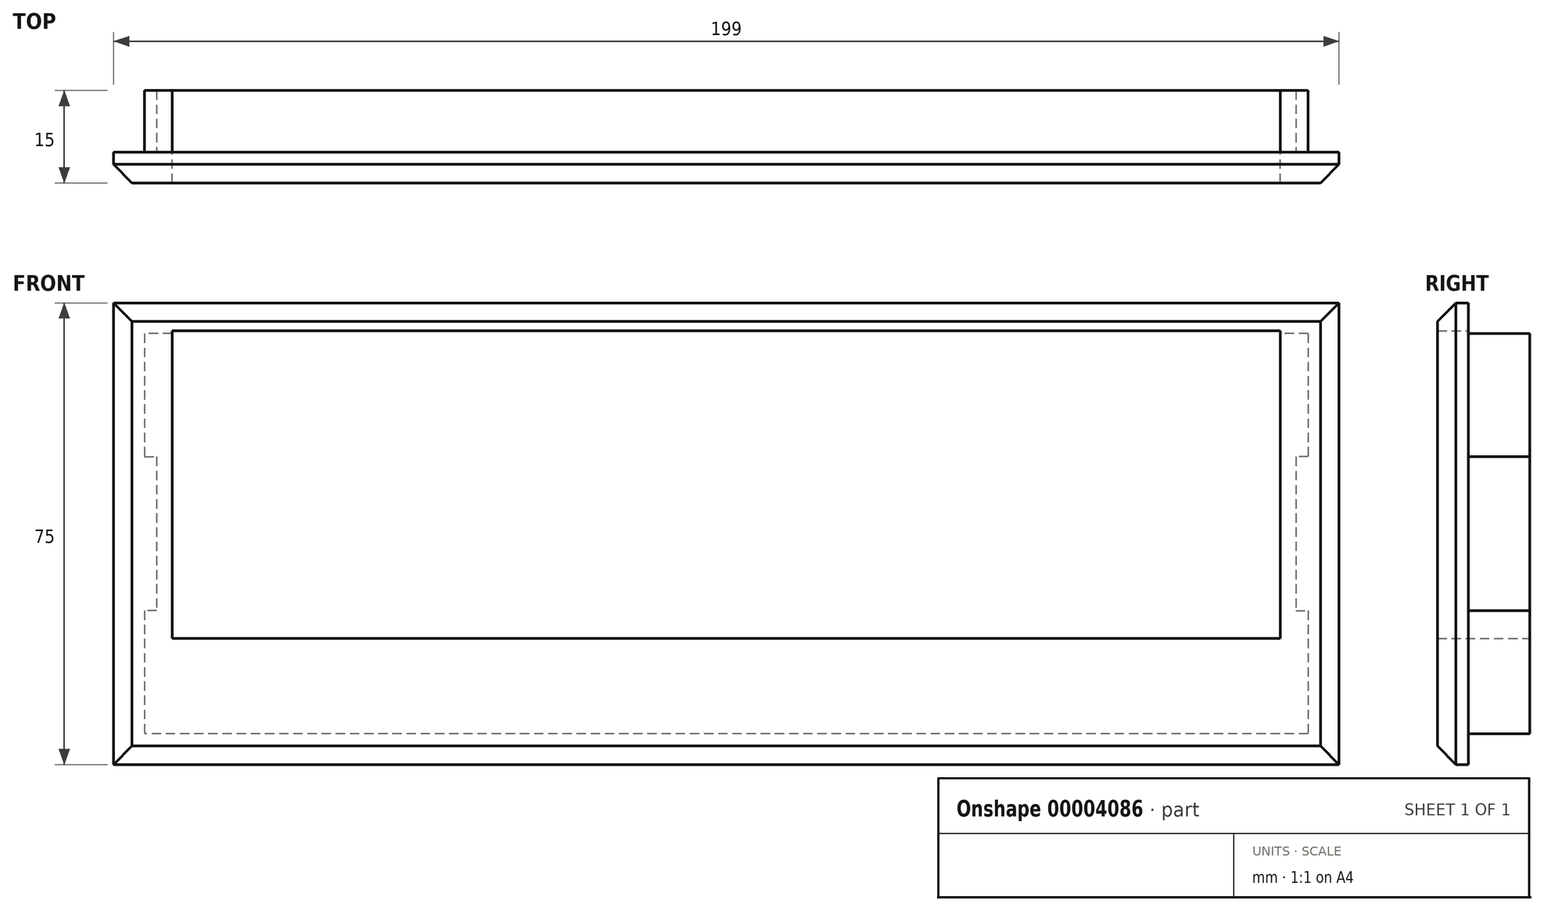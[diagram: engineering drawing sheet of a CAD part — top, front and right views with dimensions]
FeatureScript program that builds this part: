
annotation { "Feature Type Name" : "Feature", "Feature Type Description" : "" }
export const myFeature = defineFeature(function(context is Context, id is Id, definition is map)
    precondition{}
    {
        {
            var Q0;
            Q0=qCreatedBy(makeId("Front.planeOp"),FACE);
            var sketch = newSketch(context, id + "F0", { "sketchPlane" : qUnion([Q0])});
            skLineSegment(sketch, "E0.rect.bottom", {"start": v(94.5, 32.5) * mm, "end": v(-94.5, 32.5) * mm});
            skLineSegment(sketch, "E0.rect.top", {"start": v(94.5, -32.5) * mm, "end": v(-94.5, -32.5) * mm});
            skLineSegment(sketch, "E0.rect.left", {"start": v(94.5, 32.5) * mm, "end": v(94.5, 12.5) * mm});
            skLineSegment(sketch, "E0.rect.right", {"start": v(-94.5, 32.5) * mm, "end": v(-94.5, 12.5) * mm});
            skPoint(sketch, "E0.rect.middle", {"position": v(0, 0) * mm});
            skLineSegment(sketch, "E1", {"start": v(-94.5, 12.5) * mm, "end": v(-92.5, 12.5) * mm});
            skLineSegment(sketch, "E2", {"start": v(-92.5, 12.5) * mm, "end": v(-92.5, -12.5) * mm});
            skLineSegment(sketch, "E3", {"start": v(-92.5, -12.5) * mm, "end": v(-94.5, -12.5) * mm});
            skLineSegment(sketch, "E4.trimOffspring", {"start": v(-94.5, -12.5) * mm, "end": v(-94.5, -32.5) * mm});
            skLineSegment(sketch, "E5", {"start": v(94.5, 12.5) * mm, "end": v(92.5, 12.5) * mm});
            skLineSegment(sketch, "E6", {"start": v(92.5, 12.5) * mm, "end": v(92.5, -12.5) * mm});
            skLineSegment(sketch, "E7", {"start": v(92.5, -12.5) * mm, "end": v(94.5, -12.5) * mm});
            skLineSegment(sketch, "E8.trimOffspring", {"start": v(94.5, -12.5) * mm, "end": v(94.5, -32.5) * mm});
            skSolve(sketch);
        }
        {
            var Q0;
            Q0 = qSketchRegion(id + "F0", true);
            extrude(context, id + "F1", {"entities" : qUnion([Q0]), "oppositeDirection" : true, "depth" : 10 * mm});
        }
        {
            var Q0;
            Q0=makeQuery(id+"F1.opExtrude","CAP_FACE",FACE,{"disambiguationData":[OSD([sQuery(id+"F0.wireOp",EDGE,"E0.rect.bottom"),sQuery(id+"F0.wireOp",EDGE,"E0.rect.top"),sQuery(id+"F0.wireOp",EDGE,"E0.rect.left"),sQuery(id+"F0.wireOp",EDGE,"E0.rect.right"),sQuery(id+"F0.wireOp",EDGE,"E1"),sQuery(id+"F0.wireOp",EDGE,"E2"),sQuery(id+"F0.wireOp",EDGE,"E3"),sQuery(id+"F0.wireOp",EDGE,"E4.trimOffspring"),sQuery(id+"F0.wireOp",EDGE,"E5"),sQuery(id+"F0.wireOp",EDGE,"E6"),sQuery(id+"F0.wireOp",EDGE,"E7"),sQuery(id+"F0.wireOp",EDGE,"E8.trimOffspring")])],"isStart":true});
            var sketch = newSketch(context, id + "F2", { "sketchPlane" : qUnion([Q0])});
            skLineSegment(sketch, "E9.rect.bottom", {"start": v(99.5, -37.5) * mm, "end": v(-99.5, -37.5) * mm});
            skLineSegment(sketch, "E9.rect.top", {"start": v(99.5, 37.5) * mm, "end": v(-99.5, 37.5) * mm});
            skLineSegment(sketch, "E9.rect.left", {"start": v(99.5, -37.5) * mm, "end": v(99.5, 37.5) * mm});
            skLineSegment(sketch, "E9.rect.right", {"start": v(-99.5, -37.5) * mm, "end": v(-99.5, 37.5) * mm});
            skPoint(sketch, "E9.rect.middle", {"position": v(0, 0) * mm});
            skSolve(sketch);
        }
        {
            var Q0;
            Q0 = qSketchRegion(id + "F2", true);
            extrude(context, id + "F3", {"entities" : qUnion([Q0]), "operationType" : NewBodyOperationType.ADD, "depth" : 5 * mm});
        }
        {
            var Q0;
            Q0=makeQuery(id+"F1.opExtrude","CAP_FACE",FACE,{"disambiguationData":[OSD([sQuery(id+"F0.wireOp",EDGE,"E0.rect.bottom"),sQuery(id+"F0.wireOp",EDGE,"E0.rect.top"),sQuery(id+"F0.wireOp",EDGE,"E0.rect.left"),sQuery(id+"F0.wireOp",EDGE,"E0.rect.right"),sQuery(id+"F0.wireOp",EDGE,"E1"),sQuery(id+"F0.wireOp",EDGE,"E2"),sQuery(id+"F0.wireOp",EDGE,"E3"),sQuery(id+"F0.wireOp",EDGE,"E4.trimOffspring"),sQuery(id+"F0.wireOp",EDGE,"E5"),sQuery(id+"F0.wireOp",EDGE,"E6"),sQuery(id+"F0.wireOp",EDGE,"E7"),sQuery(id+"F0.wireOp",EDGE,"E8.trimOffspring")])],"isStart":false});
            var sketch = newSketch(context, id + "F4", { "sketchPlane" : qUnion([Q0])});
            skLineSegment(sketch, "E10.rect.bottom", {"start": v(90, -17) * mm, "end": v(-90, -17) * mm});
            skLineSegment(sketch, "E10.rect.top", {"start": v(90, 33) * mm, "end": v(-90, 33) * mm});
            skLineSegment(sketch, "E10.rect.left", {"start": v(90, -17) * mm, "end": v(90, 33) * mm});
            skLineSegment(sketch, "E10.rect.right", {"start": v(-90, -17) * mm, "end": v(-90, 33) * mm});
            skPoint(sketch, "E10.rect.middle", {"position": v(0, 8) * mm});
            skSolve(sketch);
        }
        {
            var Q0;
            Q0 = qSketchRegion(id + "F4", true);
            extrude(context, id + "F5", {"entities" : qUnion([Q0]), "operationType" : NewBodyOperationType.REMOVE, "endBound" : BoundingType.THROUGH_ALL, "oppositeDirection" : true, "depth" : 25 * mm});
        }
        {
            var Q0;
            Q0=makeQuery(id+"F3.opExtrude","CAP_EDGE",EDGE,{"disambiguationData":[OSD([sQuery(id+"F2.wireOp",EDGE,"E9.rect.top")])],"isStart":false});
            var Q1;
            Q1=makeQuery(id+"F3.opExtrude","CAP_EDGE",EDGE,{"disambiguationData":[OSD([sQuery(id+"F2.wireOp",EDGE,"E9.rect.right")])],"isStart":false});
            var Q2;
            Q2=makeQuery(id+"F3.opExtrude","CAP_EDGE",EDGE,{"disambiguationData":[OSD([sQuery(id+"F2.wireOp",EDGE,"E9.rect.bottom")])],"isStart":false});
            var Q3;
            Q3=makeQuery(id+"F3.opExtrude","CAP_EDGE",EDGE,{"disambiguationData":[OSD([sQuery(id+"F2.wireOp",EDGE,"E9.rect.left")])],"isStart":false});
            chamfer(context, id + "F6", {"entities" : qUnion([Q0, Q1, Q2, Q3]), "width" : 3 * mm, "tangentPropagation" : true});
        }
    });
